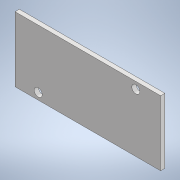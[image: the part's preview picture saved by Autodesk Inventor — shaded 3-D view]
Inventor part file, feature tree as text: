
AUTODESK INVENTOR PART (.ipt)
format: ipt  version: 2022 (Build 260153070, 153G)  size: 98,816 bytes
history: native  units: mm
features: extrude x1, sketch x1
ambient origin geometry x8: Origin, YZ Plane, XZ Plane, XY Plane, X Axis, Y Axis, Z Axis, Center Point
bodies: Solid1 (feature_tree)
feature tree (2):
  extrude  "Extrusion1"  Depth=24.2mm
  sketch  "Sketch1"  dims[d0=54.2mm d1=24.2mm d2=3.0mm d3=2.5mm d4=9.25mm d5=2.5mm d6=8.6mm d7=1.6mm d8=0.0mm]
